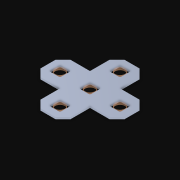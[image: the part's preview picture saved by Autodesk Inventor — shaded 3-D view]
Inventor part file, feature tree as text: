
AUTODESK INVENTOR PART (.ipt)
format: ipt  version: 2021 (Build 250183000, 183)  size: 205,312 bytes
history: native  units: in
note: dims shown in document units (in); Inventor stores cm internally (conversion verified against a paired STEP export)
features: other x6, extrude x5, pattern_linear x2, imported_body x1, sketch x1
ambient origin geometry x8: Origin, YZ Plane, XZ Plane, XY Plane, X Axis, Y Axis, Z Axis, Center Point
bodies: Body1 (feature_tree), Body2 (feature_tree), Body3 (feature_tree), Body4 (feature_tree), Body5 (feature_tree), Body6 (feature_tree)
feature tree (15):
  parser-record x1  (decoder bookkeeping rows leaked as tree rows — omitted from the tree; the rows remain in map.json)
  imported_body  "Base1"
  pattern_linear  "Rectangular Pattern1"  Count1=3 Spacing1=0.5in
  pattern_linear  "Rectangular Pattern2"  Spacing1=0.046in  [1 undecoded]
  other  "Srf1"
  other  "Srf2"
  other  "Srf3"
  sketch  "Sketch2"  dims[d15=0.046in d16=0.0in d17=1.1811in d19=0.5in d21=0.046in d22=0.0in d23=0.7874in d25=1.0in]
  other  "Srf4"
  other  "Srf5"
  extrude  "ExtrusionSrf1"  Depth=1.0in
  extrude  "ExtrusionSrf4"  [1 undecoded]
  extrude  "ExtrusionSrf2"  [1 undecoded]
  extrude  "ExtrusionSrf3"  [1 undecoded]
  extrude  "ExtrusionSrf5"  [1 undecoded]
note: 5 required parameter values undecoded (feature->parameter linkage not recoverable at this tier; creation-order binding heuristic only, values carry confidence <= 0.55)
